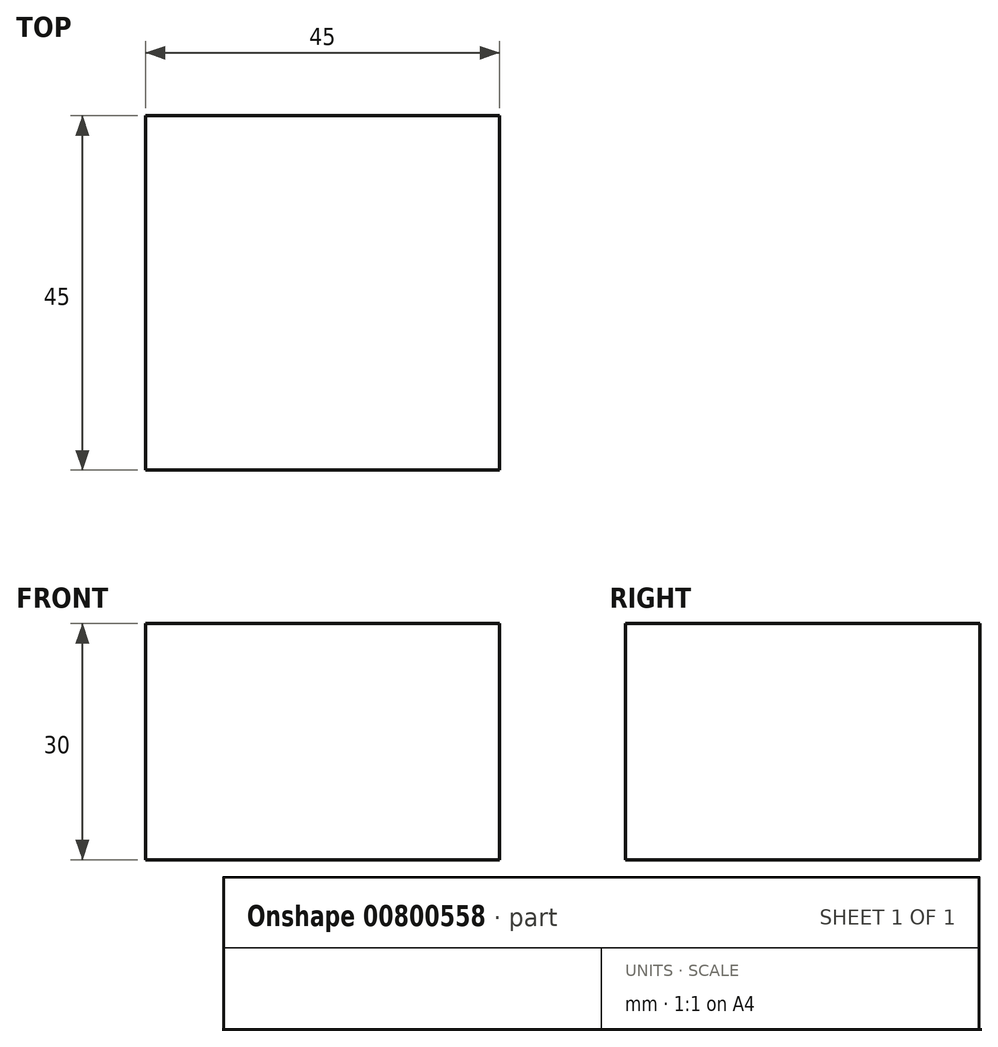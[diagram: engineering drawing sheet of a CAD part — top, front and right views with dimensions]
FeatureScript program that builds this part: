
annotation { "Feature Type Name" : "Feature", "Feature Type Description" : "" }
export const myFeature = defineFeature(function(context is Context, id is Id, definition is map)
    precondition{}
    {
        {
            var Q0;
            Q0=qCreatedBy(makeId("Front.planeOp"),FACE);
            var sketch = newSketch(context, id + "F0", { "sketchPlane" : qUnion([Q0])});
            skLineSegment(sketch, "E0.bottom", {"start": v(-33, 42) * mm, "end": v(12, 42) * mm});
            skLineSegment(sketch, "E0.top", {"start": v(-33, 12) * mm, "end": v(12, 12) * mm});
            skLineSegment(sketch, "E0.left", {"start": v(-33, 42) * mm, "end": v(-33, 12) * mm});
            skLineSegment(sketch, "E0.right", {"start": v(12, 42) * mm, "end": v(12, 12) * mm});
            skSolve(sketch);
        }
        {
            var Q0;
            Q0=makeQuery(id+"F0.imprint","IMPRINT",FACE,{"disambiguationData":[TD([[makeQuery(id+"F0.imprint","IMPRINT",EDGE,{"derivedFrom":sQuery(id+"F0.wireOp",EDGE,"E0.bottom")}),-1.0]])]});
            extrude(context, id + "F1", {"entities" : qUnion([Q0]), "depth" : 45 * mm, "offsetDistance" : 25 * mm});
        }
    });
